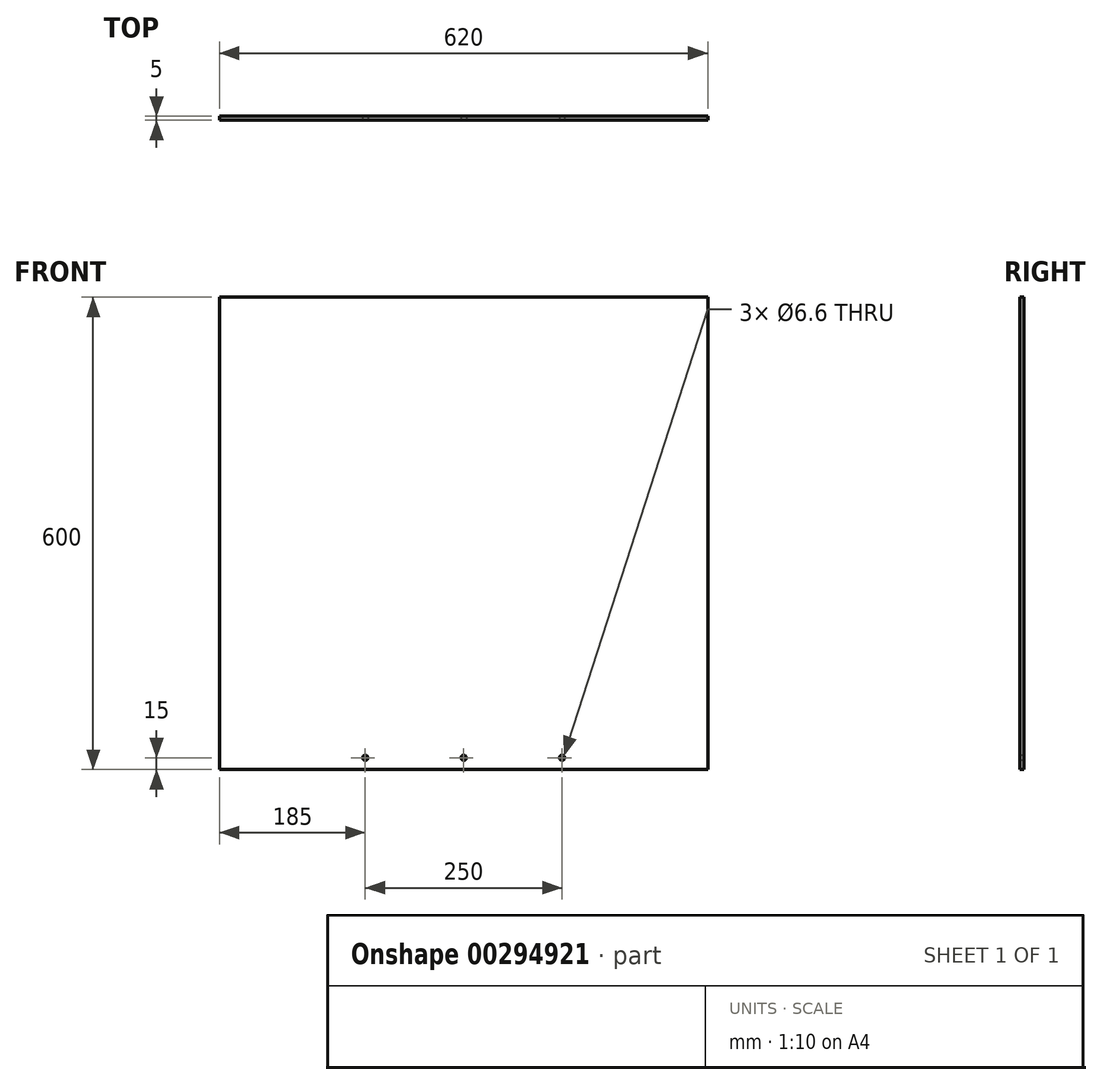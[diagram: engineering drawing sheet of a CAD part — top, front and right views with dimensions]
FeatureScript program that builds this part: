
annotation { "Feature Type Name" : "Feature", "Feature Type Description" : "" }
export const myFeature = defineFeature(function(context is Context, id is Id, definition is map)
    precondition{}
    {
        {
            var Q0;
            Q0=qCreatedBy(makeId("Front.planeOp"),FACE);
            var sketch = newSketch(context, id + "F0", { "sketchPlane" : qUnion([Q0])});
            skLineSegment(sketch, "E0.bottom", {"start": v(-310, 300) * mm, "end": v(310, 300) * mm});
            skLineSegment(sketch, "E0.top", {"start": v(-310, -300) * mm, "end": v(310, -300) * mm});
            skLineSegment(sketch, "E0.left", {"start": v(-310, 300) * mm, "end": v(-310, -300) * mm});
            skLineSegment(sketch, "E0.right", {"start": v(310, 300) * mm, "end": v(310, -300) * mm});
            skPoint(sketch, "E0.middle", {"position": v(0, 0) * mm});
            skLineSegment(sketch, "E1", {"start": v(-250, 300) * mm, "end": v(-250, -300) * mm, "construction": true});
            skLineSegment(sketch, "E2", {"start": v(-310, -100) * mm, "end": v(310, -100) * mm, "construction": true});
            skSolve(sketch);
        }
        {
            var Q0;
            {var subQ1=sQuery(id+"F0.wireOp",EDGE,"E0.top");Q0=makeQuery(id+"F0.imprint","IMPRINT",FACE,{"disambiguationData":[TD([[makeQuery(id+"F0.imprint","IMPRINT",EDGE,{"derivedFrom":subQ1}),1.0]])]});}
            extrude(context, id + "F1", {"entities" : qUnion([Q0]), "depth" : 5 * mm, "offsetDistance" : 25 * mm});
        }
        {
            var Q0;
            Q0=makeQuery(id+"F1.opExtrude","CAP_FACE",FACE,{"disambiguationData":[OSD([sQuery(id+"F0.wireOp",EDGE,"E0.bottom"),sQuery(id+"F0.wireOp",EDGE,"E0.top"),sQuery(id+"F0.wireOp",EDGE,"E0.left"),sQuery(id+"F0.wireOp",EDGE,"E0.right"),sQuery(id+"F0.wireOp",EDGE,"YRUpu2Rf-bW4s-S1CS-utQ9-MKq874qqm9uK")])],"isStart":false});
            var sketch = newSketch(context, id + "F2", { "sketchPlane" : qUnion([Q0])});
            skLineSegment(sketch, "E3", {"start": v(-310, -285) * mm, "end": v(310, -285) * mm, "construction": true});
            skPoint(sketch, "E4", {"position": v(-125, -285) * mm});
            skPoint(sketch, "E5", {"position": v(125, -285) * mm});
            skPoint(sketch, "E6", {"position": v(0, -285) * mm});
            skLineSegment(sketch, "E7", {"start": v(-250, 300) * mm, "end": v(-250, -300) * mm, "construction": true});
            skSolve(sketch);
        }
        {
            var Q0;
            Q0=sQuery(id+"F2.wireOp",VERTEX,"E4");
            var Q1;
            Q1=sQuery(id+"F2.wireOp",VERTEX,"29e96742-76e6-4ba6-ab32-156a816730d5");
            var Q2;
            Q2=sQuery(id+"F2.wireOp",VERTEX,"E5");
            var Q3;
            Q3=sQuery(id+"F2.wireOp",VERTEX,"E6");
            var Q4;
            Q4=makeQuery(id+"F1.opExtrude","SWEPT_BODY",BODY,{"disambiguationData":[OSD([sQuery(id+"F0.wireOp",EDGE,"E0.bottom"),sQuery(id+"F0.wireOp",EDGE,"E0.top"),sQuery(id+"F0.wireOp",EDGE,"E0.left"),sQuery(id+"F0.wireOp",EDGE,"E0.right"),sQuery(id+"F0.wireOp",EDGE,"YRUpu2Rf-bW4s-S1CS-utQ9-MKq874qqm9uK")])]});
            hole(context, id + "F3", {"style" : HoleStyle.SIMPLE, "endStyle" : HoleEndStyle.THROUGH, "standardTappedOrClearance" : lookupTablePath({ "standard" : "ISO", "fit" : "Normal", "size" : "M6", "type" : "Clearance" }), "standardBlindInLast" : lookupTablePath({ "fit" : "Standard", "standard" : "ISO", "size" : "M6", "type" : "Clearance" }), "holeDiameter" : 6.6 * mm, "isTappedThrough" : true, "tappedDepth" : 12 * mm, "tapClearance" : 3, "locations" : qUnion([Q0, Q1, Q2, Q3]), "scope" : qUnion([Q4])});
        }
    });
